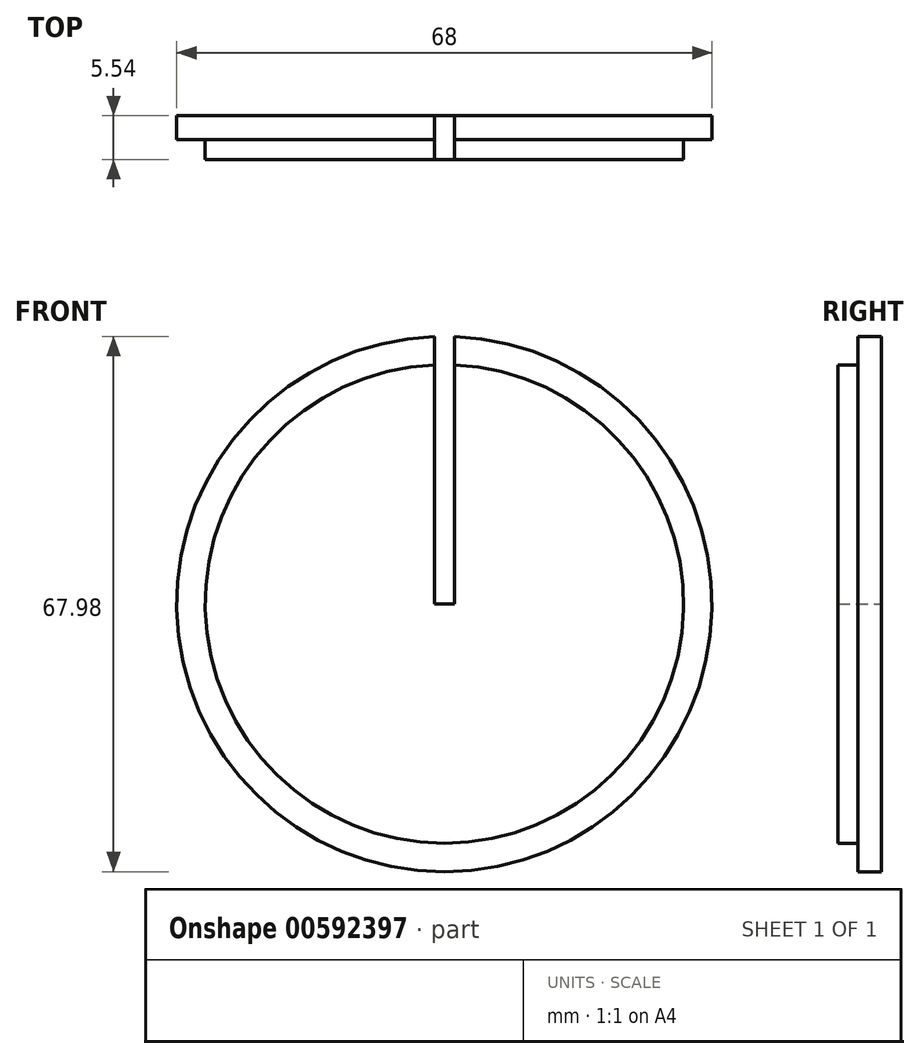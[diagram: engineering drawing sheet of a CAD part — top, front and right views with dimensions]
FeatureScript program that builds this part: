
annotation { "Feature Type Name" : "Feature", "Feature Type Description" : "" }
export const myFeature = defineFeature(function(context is Context, id is Id, definition is map)
    precondition{}
    {
        {
            var Q0;
            Q0=qCreatedBy(makeId("Front.planeOp"),FACE);
            var sketch = newSketch(context, id + "F0", { "sketchPlane" : qUnion([Q0])});
            skCircle(sketch, "E0", {"center": v(0, 0) * mm, "radius": 34 * mm});
            skSolve(sketch);
        }
        {
            var Q0;
            Q0=makeQuery(id+"F0.imprint","IMPRINT",FACE,{"disambiguationData":[TD([[makeQuery(id+"F0.imprint","IMPRINT",EDGE,{"derivedFrom":sQuery(id+"F0.wireOp",EDGE,"E0")}),1.0]])]});
            extrude(context, id + "F1", {"entities" : qUnion([Q0]), "depth" : 3 * mm, "offsetDistance" : 25.4 * mm});
        }
        {
            var Q0;
            Q0=makeQuery(id+"F1.opExtrude","CAP_FACE",FACE,{"disambiguationData":[OSD([sQuery(id+"F0.wireOp",EDGE,"E0")])],"isStart":false});
            var sketch = newSketch(context, id + "F2", { "sketchPlane" : qUnion([Q0])});
            skCircle(sketch, "E1.0", {"center": v(0, 0) * mm, "radius": 30.38 * mm});
            skSolve(sketch);
        }
        {
            var Q0;
            Q0=makeQuery(id+"F2.imprint","IMPRINT",FACE,{"disambiguationData":[TD([[makeQuery(id+"F2.imprint","IMPRINT",EDGE,{"derivedFrom":sQuery(id+"F2.wireOp",EDGE,"E1.0")}),1.0]])]});
            extrude(context, id + "F3", {"entities" : qUnion([Q0]), "operationType" : NewBodyOperationType.ADD, "depth" : 2.54 * mm, "offsetDistance" : 25.4 * mm});
        }
        {
            var Q0;
            Q0=makeQuery(id+"F1.opExtrude","CAP_FACE",FACE,{"disambiguationData":[OSD([sQuery(id+"F0.wireOp",EDGE,"E0")])],"isStart":true});
            var sketch = newSketch(context, id + "F4", { "sketchPlane" : qUnion([Q0])});
            skLineSegment(sketch, "E2", {"start": v(0, 0) * mm, "end": v(1.27, 0) * mm});
            skLineSegment(sketch, "E3", {"start": v(1.27, 0) * mm, "end": v(1.27, 33.98) * mm});
            skLineSegment(sketch, "E4", {"start": v(0, 0) * mm, "end": v(-1.27, 0) * mm});
            skLineSegment(sketch, "E5", {"start": v(-1.27, 0) * mm, "end": v(-1.27, 33.98) * mm});
            skSolve(sketch);
        }
        {
            var Q0;
            Q0=makeQuery(id+"F4.imprint","IMPRINT",FACE,{"disambiguationData":[TD([[makeQuery(id+"F4.imprint","IMPRINT",EDGE,{"derivedFrom":sQuery(id+"F4.wireOp",EDGE,"E2")}),1.0]])]});
            extrude(context, id + "F5", {"entities" : qUnion([Q0]), "operationType" : NewBodyOperationType.REMOVE, "oppositeDirection" : true, "depth" : 25.4 * mm, "offsetDistance" : 25.4 * mm});
        }
    });
